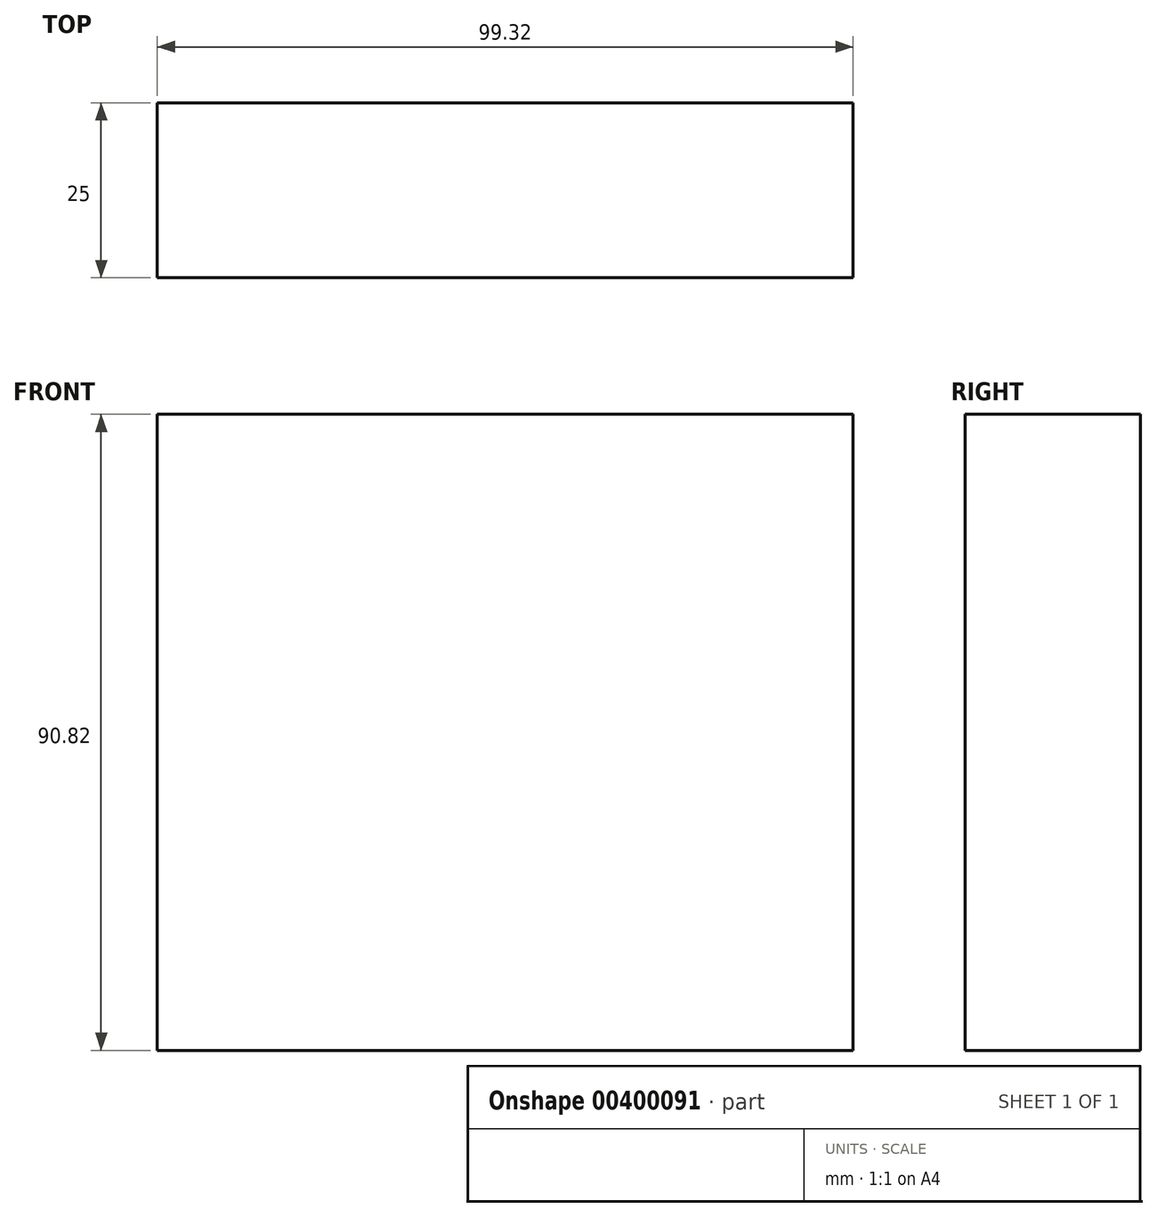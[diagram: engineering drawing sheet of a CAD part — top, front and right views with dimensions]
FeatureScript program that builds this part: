
annotation { "Feature Type Name" : "Feature", "Feature Type Description" : "" }
export const myFeature = defineFeature(function(context is Context, id is Id, definition is map)
    precondition{}
    {
        {
            var Q0;
            Q0=qCreatedBy(makeId("Front.planeOp"),FACE);
            var sketch = newSketch(context, id + "F0", { "sketchPlane" : qUnion([Q0])});
            skLineSegment(sketch, "E0.bottom", {"start": v(49.66, 45.4) * mm, "end": v(-49.66, 45.4) * mm});
            skLineSegment(sketch, "E0.top", {"start": v(49.66, -45.4) * mm, "end": v(-49.66, -45.4) * mm});
            skLineSegment(sketch, "E0.left", {"start": v(49.66, 45.4) * mm, "end": v(49.66, -45.4) * mm});
            skLineSegment(sketch, "E0.right", {"start": v(-49.66, 45.4) * mm, "end": v(-49.66, -45.4) * mm});
            skPoint(sketch, "E0.middle", {"position": v(0, 0) * mm});
            skSolve(sketch);
        }
        {
            var Q0;
            Q0=makeQuery(id+"F0.imprint","IMPRINT",FACE,{"disambiguationData":[TD([[makeQuery(id+"F0.imprint","IMPRINT",EDGE,{"derivedFrom":sQuery(id+"F0.wireOp",EDGE,"E0.bottom")}),1.0]])]});
            var Q1;
            Q1=makeQuery(id+"F0.imprint","IMPRINT",FACE,{"disambiguationData":[TD([[makeQuery(id+"F0.imprint","IMPRINT",EDGE,{"derivedFrom":sQuery(id+"F0.wireOp",EDGE,"E0.bottom")}),1.0]])]});
            extrude(context, id + "F1", {"entities" : qUnion([Q0, Q1]), "depth" : 25 * mm});
        }
    });
